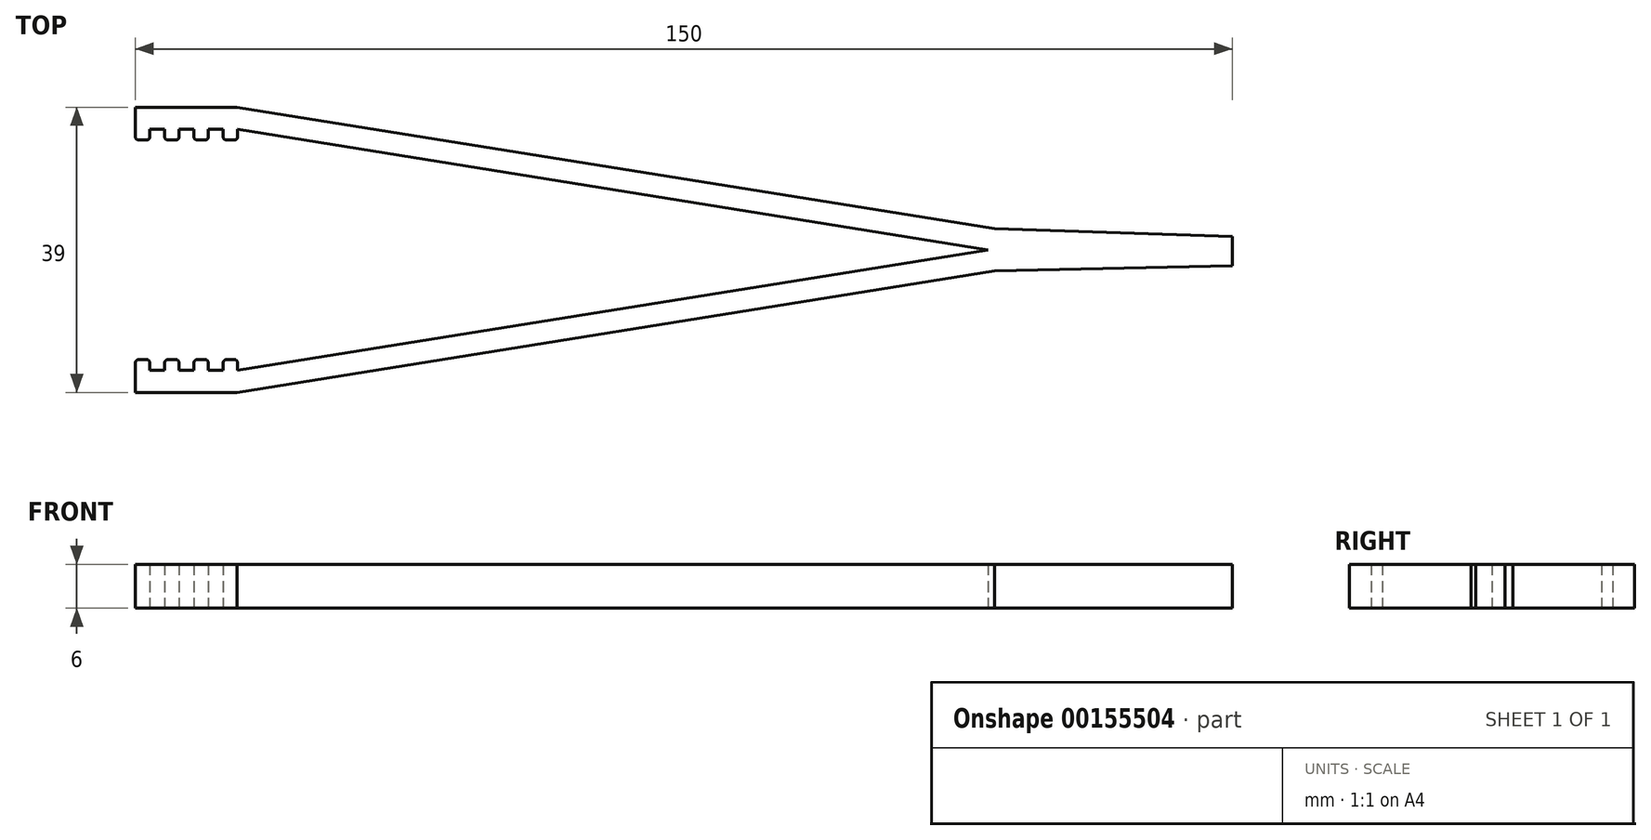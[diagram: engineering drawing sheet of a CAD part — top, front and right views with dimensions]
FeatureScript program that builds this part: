
annotation { "Feature Type Name" : "Feature", "Feature Type Description" : "" }
export const myFeature = defineFeature(function(context is Context, id is Id, definition is map)
    precondition{}
    {
        {
            var Q0;
            Q0=qCreatedBy(makeId("Top.planeOp"),FACE);
            var sketch = newSketch(context, id + "F0", { "sketchPlane" : qUnion([Q0])});
            skLineSegment(sketch, "E0", {"start": v(75.91, -2.87) * mm, "end": v(-27.63, -19.5) * mm});
            skLineSegment(sketch, "E1", {"start": v(-27.63, -19.5) * mm, "end": v(-41.56, -19.5) * mm});
            skLineSegment(sketch, "E2", {"start": v(-41.56, -19.5) * mm, "end": v(-41.56, -15.5) * mm});
            skLineSegment(sketch, "E3", {"start": v(-41.06, -15) * mm, "end": v(-40.06, -15) * mm});
            skLineSegment(sketch, "E4", {"start": v(-39.56, -15.5) * mm, "end": v(-39.56, -16.5) * mm});
            skLineSegment(sketch, "E5", {"start": v(-39.56, -16.5) * mm, "end": v(-37.56, -16.5) * mm});
            skLineSegment(sketch, "E6", {"start": v(-37.56, -16.5) * mm, "end": v(-37.56, -15.5) * mm});
            skLineSegment(sketch, "E7", {"start": v(-37.06, -15) * mm, "end": v(-36.06, -15) * mm});
            skLineSegment(sketch, "E8", {"start": v(-35.56, -15.5) * mm, "end": v(-35.56, -16.5) * mm});
            skLineSegment(sketch, "E9", {"start": v(-35.56, -16.5) * mm, "end": v(-33.56, -16.5) * mm});
            skLineSegment(sketch, "E10", {"start": v(-33.56, -16.5) * mm, "end": v(-33.56, -15.5) * mm});
            skLineSegment(sketch, "E11", {"start": v(-33.06, -15) * mm, "end": v(-32.06, -15) * mm});
            skLineSegment(sketch, "E12", {"start": v(-31.56, -15.5) * mm, "end": v(-31.56, -16.5) * mm});
            skLineSegment(sketch, "E13", {"start": v(-31.56, -16.5) * mm, "end": v(-29.56, -16.5) * mm});
            skLineSegment(sketch, "E14", {"start": v(-29.56, -16.5) * mm, "end": v(-29.56, -15.5) * mm});
            skLineSegment(sketch, "E15", {"start": v(-29.06, -15) * mm, "end": v(-28.06, -15) * mm});
            skLineSegment(sketch, "E16", {"start": v(-27.56, -15.5) * mm, "end": v(-27.56, -16.5) * mm});
            skLineSegment(sketch, "E17", {"start": v(-27.56, -16.5) * mm, "end": v(75.04, 0) * mm});
            skPoint(sketch, "E18.visualSharp", {"position": v(-41.56, -15) * mm});
            skArc(sketch, "E18.filletArc", {"start": v(-41.06, -15) * mm, "mid": v(-41.42, -15.15) * mm, "end": v(-41.56, -15.5) * mm});
            skPoint(sketch, "E19.visualSharp", {"position": v(-39.56, -15) * mm});
            skArc(sketch, "E19.filletArc", {"start": v(-39.56, -15.5) * mm, "mid": v(-39.71, -15.15) * mm, "end": v(-40.06, -15) * mm});
            skPoint(sketch, "E20.visualSharp", {"position": v(-37.56, -15) * mm});
            skArc(sketch, "E20.filletArc", {"start": v(-37.06, -15) * mm, "mid": v(-37.42, -15.15) * mm, "end": v(-37.56, -15.5) * mm});
            skPoint(sketch, "E21.visualSharp", {"position": v(-35.56, -15) * mm});
            skArc(sketch, "E21.filletArc", {"start": v(-35.56, -15.5) * mm, "mid": v(-35.71, -15.15) * mm, "end": v(-36.06, -15) * mm});
            skPoint(sketch, "E22.visualSharp", {"position": v(-33.56, -15) * mm});
            skArc(sketch, "E22.filletArc", {"start": v(-33.06, -15) * mm, "mid": v(-33.42, -15.15) * mm, "end": v(-33.56, -15.5) * mm});
            skPoint(sketch, "E23.visualSharp", {"position": v(-31.56, -15) * mm});
            skArc(sketch, "E23.filletArc", {"start": v(-31.56, -15.5) * mm, "mid": v(-31.71, -15.15) * mm, "end": v(-32.06, -15) * mm});
            skPoint(sketch, "E24.visualSharp", {"position": v(-29.56, -15) * mm});
            skArc(sketch, "E24.filletArc", {"start": v(-29.06, -15) * mm, "mid": v(-29.42, -15.15) * mm, "end": v(-29.56, -15.5) * mm});
            skPoint(sketch, "E25.visualSharp", {"position": v(-27.56, -15) * mm});
            skArc(sketch, "E25.filletArc", {"start": v(-27.56, -15.5) * mm, "mid": v(-27.71, -15.15) * mm, "end": v(-28.06, -15) * mm});
            skLineSegment(sketch, "E26", {"start": v(-27.56, -16.5) * mm, "end": v(-27.63, -19.5) * mm, "construction": true});
            skArc(sketch, "E27.MirrorCS", {"start": v(-39.56, 15.5) * mm, "mid": v(-39.71, 15.15) * mm, "end": v(-40.06, 15) * mm});
            skArc(sketch, "E28.MirrorCS", {"start": v(-41.06, 15) * mm, "mid": v(-41.42, 15.15) * mm, "end": v(-41.56, 15.5) * mm});
            skLineSegment(sketch, "E29.MirrorCS", {"start": v(-37.56, 16.5) * mm, "end": v(-37.56, 15.5) * mm});
            skLineSegment(sketch, "E30.MirrorCS", {"start": v(-35.56, 15.5) * mm, "end": v(-35.56, 16.5) * mm});
            skLineSegment(sketch, "E31.MirrorCS", {"start": v(-37.06, 15) * mm, "end": v(-36.06, 15) * mm});
            skArc(sketch, "E32.MirrorCS", {"start": v(-29.06, 15) * mm, "mid": v(-29.42, 15.15) * mm, "end": v(-29.56, 15.5) * mm});
            skLineSegment(sketch, "E33.MirrorCS", {"start": v(-27.56, 15.5) * mm, "end": v(-27.56, 16.5) * mm});
            skLineSegment(sketch, "E34.MirrorCS", {"start": v(-41.06, 15) * mm, "end": v(-40.06, 15) * mm});
            skArc(sketch, "E35.MirrorCS", {"start": v(-33.06, 15) * mm, "mid": v(-33.42, 15.15) * mm, "end": v(-33.56, 15.5) * mm});
            skArc(sketch, "E36.MirrorCS", {"start": v(-31.56, 15.5) * mm, "mid": v(-31.71, 15.15) * mm, "end": v(-32.06, 15) * mm});
            skLineSegment(sketch, "E37.MirrorCS", {"start": v(-39.56, 15.5) * mm, "end": v(-39.56, 16.5) * mm});
            skArc(sketch, "E38.MirrorCS", {"start": v(-37.06, 15) * mm, "mid": v(-37.42, 15.15) * mm, "end": v(-37.56, 15.5) * mm});
            skArc(sketch, "E39.MirrorCS", {"start": v(-35.56, 15.5) * mm, "mid": v(-35.71, 15.15) * mm, "end": v(-36.06, 15) * mm});
            skLineSegment(sketch, "E40.MirrorCS", {"start": v(-29.06, 15) * mm, "end": v(-28.06, 15) * mm});
            skLineSegment(sketch, "E41.MirrorCS", {"start": v(-31.56, 15.5) * mm, "end": v(-31.56, 16.5) * mm});
            skArc(sketch, "E42.MirrorCS", {"start": v(-27.56, 15.5) * mm, "mid": v(-27.71, 15.15) * mm, "end": v(-28.06, 15) * mm});
            skLineSegment(sketch, "E43.MirrorCS", {"start": v(-33.06, 15) * mm, "end": v(-32.06, 15) * mm});
            skLineSegment(sketch, "E44.MirrorCS", {"start": v(-29.56, 16.5) * mm, "end": v(-29.56, 15.5) * mm});
            skLineSegment(sketch, "E45.MirrorCS", {"start": v(-33.56, 16.5) * mm, "end": v(-33.56, 15.5) * mm});
            skLineSegment(sketch, "E46.MirrorCS", {"start": v(-39.56, 16.5) * mm, "end": v(-37.56, 16.5) * mm});
            skPoint(sketch, "E47.MirrorP", {"position": v(-29.56, 15) * mm});
            skPoint(sketch, "E48.MirrorP", {"position": v(-31.56, 15) * mm});
            skLineSegment(sketch, "E49.MirrorCS", {"start": v(-31.56, 16.5) * mm, "end": v(-29.56, 16.5) * mm});
            skPoint(sketch, "E50.MirrorP", {"position": v(-37.56, 15) * mm});
            skLineSegment(sketch, "E51.MirrorCS", {"start": v(-27.56, 16.5) * mm, "end": v(-27.63, 19.5) * mm, "construction": true});
            skLineSegment(sketch, "E52.MirrorCS", {"start": v(-27.63, 19.5) * mm, "end": v(-41.56, 19.5) * mm});
            skLineSegment(sketch, "E53.MirrorCS", {"start": v(-41.56, 19.5) * mm, "end": v(-41.56, 15.5) * mm});
            skLineSegment(sketch, "E54.MirrorCS", {"start": v(-35.56, 16.5) * mm, "end": v(-33.56, 16.5) * mm});
            skPoint(sketch, "E55.MirrorP", {"position": v(-27.56, 15) * mm});
            skLineSegment(sketch, "E56.MirrorCS", {"start": v(-27.56, 16.5) * mm, "end": v(75.04, 0) * mm});
            skPoint(sketch, "E57.MirrorP", {"position": v(-41.56, 15) * mm});
            skLineSegment(sketch, "E58.MirrorCS", {"start": v(75.91, 2.87) * mm, "end": v(-27.63, 19.5) * mm});
            skPoint(sketch, "E59.MirrorP", {"position": v(-35.56, 15) * mm});
            skPoint(sketch, "E60.MirrorP", {"position": v(-33.56, 15) * mm});
            skPoint(sketch, "E61.MirrorP", {"position": v(-39.56, 15) * mm});
            skLineSegment(sketch, "E62", {"start": v(108.44, 1.8) * mm, "end": v(108.44, -2.2) * mm});
            skLineSegment(sketch, "E63", {"start": v(75.91, 2.87) * mm, "end": v(108.44, 1.8) * mm});
            skLineSegment(sketch, "E64", {"start": v(108.44, -2.2) * mm, "end": v(75.91, -2.87) * mm});
            skSolve(sketch);
        }
        {
            var Q0;
            Q0=makeQuery(id+"F0.imprint","IMPRINT",FACE,{"disambiguationData":[TD([[makeQuery(id+"F0.imprint","IMPRINT",EDGE,{"derivedFrom":sQuery(id+"F0.wireOp",EDGE,"E0")}),-1.0]])]});
            extrude(context, id + "F1", {"entities" : qUnion([Q0]), "depth" : 6 * mm});
        }
    });
